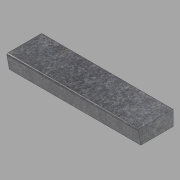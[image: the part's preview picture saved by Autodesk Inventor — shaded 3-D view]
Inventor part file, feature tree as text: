
AUTODESK INVENTOR PART (.ipt)
format: ipt  version: 2022.1 (Build 261234020, 234B)  size: 98,816 bytes
history: native  units: in
note: dims shown in document units (in); Inventor stores cm internally (conversion verified against a paired STEP export)
features: other x3, extrude x1, sketch x1
ambient origin geometry x8: Origin, YZ Plane, XZ Plane, XY Plane, X Axis, Y Axis, Z Axis, Center Point
bodies: Solid1 (feature_tree)
feature tree (5):
  other  "Blocks"
  extrude  "Extrusion1"  Depth=52.875in TaperAngle=0.0deg
  sketch  "Sketch1"  dims[d0=13.0in d1=6.0in d2=13.5in d4=0.5in d5=0.5in d6=52.875in d7=0.0in]
  other  "Profile"
  other  "Profile:1"
